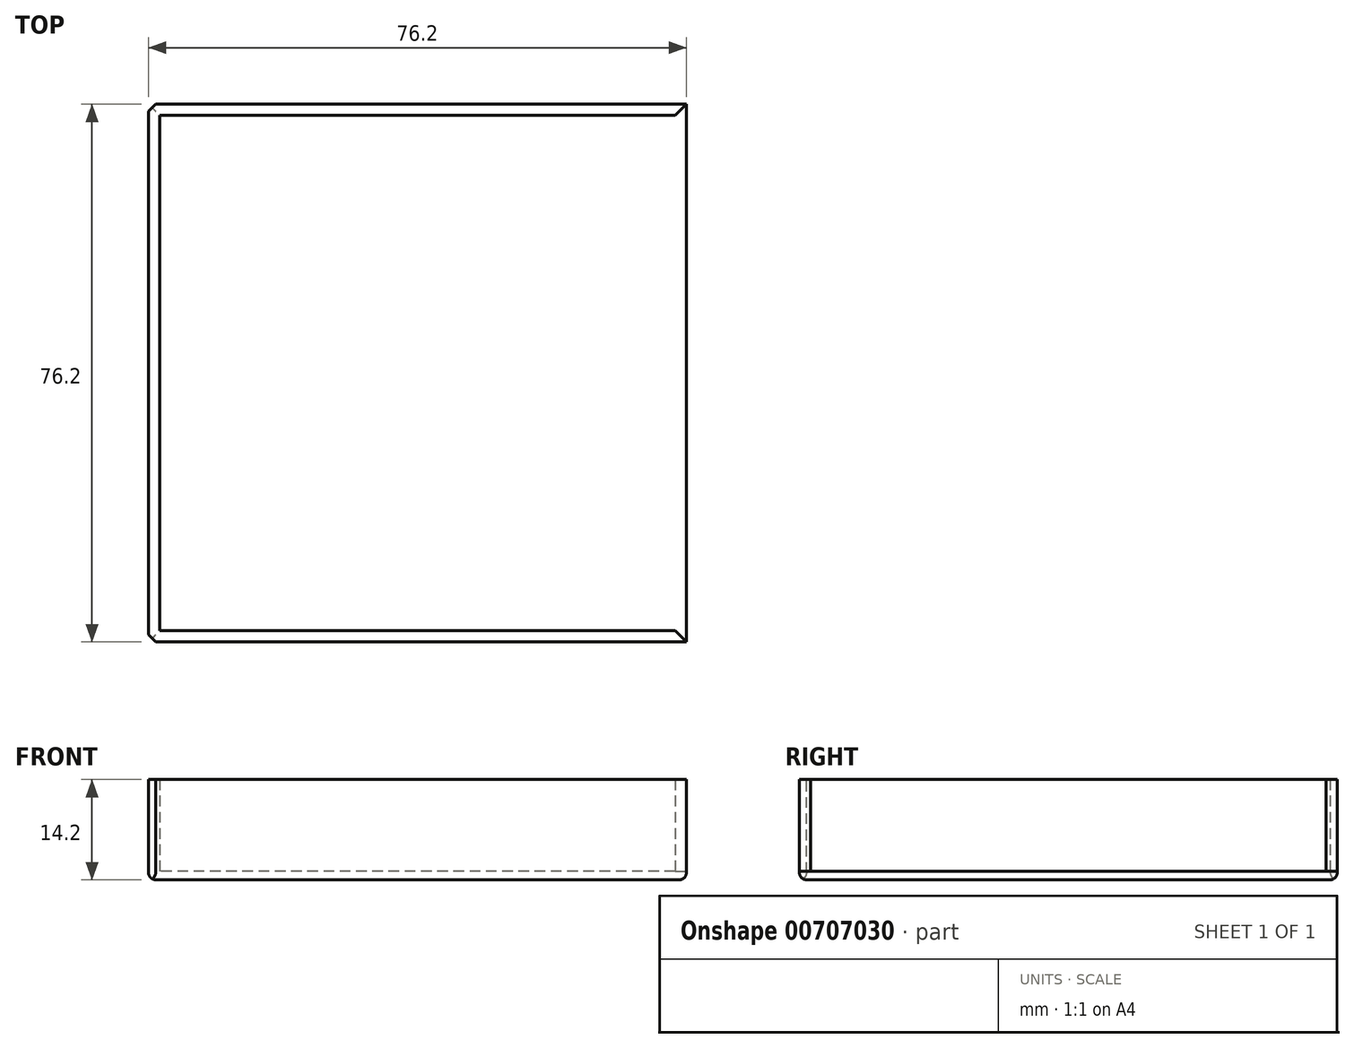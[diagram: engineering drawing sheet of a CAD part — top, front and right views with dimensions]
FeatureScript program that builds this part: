
annotation { "Feature Type Name" : "Feature", "Feature Type Description" : "" }
export const myFeature = defineFeature(function(context is Context, id is Id, definition is map)
    precondition{}
    {
        {
            var Q0;
            Q0=qCreatedBy(makeId("Top.planeOp"),FACE);
            var sketch = newSketch(context, id + "F0", { "sketchPlane" : qUnion([Q0])});
            skLineSegment(sketch, "E0.bottom", {"start": v(36.5, 36.5) * mm, "end": v(-36.5, 36.5) * mm});
            skLineSegment(sketch, "E0.top", {"start": v(36.5, -36.5) * mm, "end": v(-36.5, -36.5) * mm});
            skLineSegment(sketch, "E0.right", {"start": v(-36.5, 36.5) * mm, "end": v(-36.5, -36.5) * mm});
            skPoint(sketch, "E0.middle", {"position": v(0, 0) * mm});
            skLineSegment(sketch, "E1.bottom", {"start": v(38.1, 38.1) * mm, "end": v(-38.1, 38.1) * mm});
            skLineSegment(sketch, "E1.top", {"start": v(38.1, -38.1) * mm, "end": v(-38.1, -38.1) * mm});
            skLineSegment(sketch, "E1.right", {"start": v(-38.1, 38.1) * mm, "end": v(-38.1, -38.1) * mm});
            skLineSegment(sketch, "E2", {"start": v(36.5, 36.5) * mm, "end": v(38.1, 38.1) * mm});
            skLineSegment(sketch, "E3", {"start": v(36.5, -36.5) * mm, "end": v(38.1, -38.1) * mm});
            skSolve(sketch);
        }
        {
            var Q0;
            Q0=makeQuery(id+"F0.imprint","IMPRINT",FACE,{"disambiguationData":[TD([[makeQuery(id+"F0.imprint","IMPRINT",EDGE,{"derivedFrom":sQuery(id+"F0.wireOp",EDGE,"E0.bottom")}),-1.0]])]});
            extrude(context, id + "F1", {"entities" : qUnion([Q0]), "depth" : 13 * mm, "offsetDistance" : 25 * mm});
        }
        {
            var Q0;
            Q0=qCreatedBy(makeId("Top.planeOp"),FACE);
            var sketch = newSketch(context, id + "F2", { "sketchPlane" : qUnion([Q0])});
            skLineSegment(sketch, "E4.bottom", {"start": v(38.1, 38.1) * mm, "end": v(-38.1, 38.1) * mm});
            skLineSegment(sketch, "E4.top", {"start": v(38.1, -38.1) * mm, "end": v(-38.1, -38.1) * mm});
            skLineSegment(sketch, "E4.left", {"start": v(38.1, 38.1) * mm, "end": v(38.1, -38.1) * mm});
            skLineSegment(sketch, "E4.right", {"start": v(-38.1, 38.1) * mm, "end": v(-38.1, -38.1) * mm});
            skPoint(sketch, "E4.middle", {"position": v(0, 0) * mm});
            skSolve(sketch);
        }
        {
            var Q0;
            Q0=makeQuery(id+"F2.imprint","IMPRINT",FACE,{"disambiguationData":[TD([[makeQuery(id+"F2.imprint","IMPRINT",EDGE,{"derivedFrom":sQuery(id+"F2.wireOp",EDGE,"E4.bottom")}),1.0]])]});
            extrude(context, id + "F3", {"entities" : qUnion([Q0]), "operationType" : NewBodyOperationType.ADD, "oppositeDirection" : true, "depth" : 1.2 * mm, "offsetDistance" : 25 * mm});
        }
        {
            var Q0;
            Q0=makeQuery(id+"F3.opExtrude","CAP_EDGE",EDGE,{"disambiguationData":[OSD([sQuery(id+"F2.wireOp",EDGE,"E4.top")])],"isStart":false});
            var Q1;
            Q1=makeQuery(id+"F3.opExtrude","CAP_EDGE",EDGE,{"disambiguationData":[OSD([sQuery(id+"F2.wireOp",EDGE,"E4.left")])],"isStart":false});
            var Q2;
            Q2=makeQuery(id+"F3.opExtrude","CAP_EDGE",EDGE,{"disambiguationData":[OSD([sQuery(id+"F2.wireOp",EDGE,"E4.bottom")])],"isStart":false});
            var Q3;
            Q3=makeQuery(id+"F3.opExtrude","CAP_EDGE",EDGE,{"disambiguationData":[OSD([sQuery(id+"F2.wireOp",EDGE,"E4.right")])],"isStart":false});
            fillet(context, id + "F4", {"entities" : qUnion([Q0, Q1, Q2, Q3]), "radius" : 1 * mm, "tangentPropagation" : true, "allowEdgeOverflow" : false});
        }
        {
            var Q0;
            Q0=makeQuery(id+"F3.boolean.opBoolean","MERGE",EDGE,{"derivedFrom":[makeQuery(id+"F1.opExtrude","SWEPT_EDGE",EDGE,{"disambiguationData":[OSD([sQuery(id+"F0.wireOp",EDGE,"E1.top"),sQuery(id+"F0.wireOp",EDGE,"E1.right")])]}),makeQuery(id+"F3.opExtrude","SWEPT_EDGE",EDGE,{"disambiguationData":[OSD([sQuery(id+"F2.wireOp",EDGE,"E4.top"),sQuery(id+"F2.wireOp",EDGE,"E4.right")])]})]});
            var Q1;
            Q1=makeQuery(id+"F3.boolean.opBoolean","MERGE",EDGE,{"derivedFrom":[makeQuery(id+"F1.opExtrude","SWEPT_EDGE",EDGE,{"disambiguationData":[OSD([sQuery(id+"F0.wireOp",EDGE,"E1.bottom"),sQuery(id+"F0.wireOp",EDGE,"E1.right")])]}),makeQuery(id+"F3.opExtrude","SWEPT_EDGE",EDGE,{"disambiguationData":[OSD([sQuery(id+"F2.wireOp",EDGE,"E4.bottom"),sQuery(id+"F2.wireOp",EDGE,"E4.right")])]})]});
            chamfer(context, id + "F5", {"entities" : qUnion([Q0, Q1]), "width" : 1 * mm});
        }
    });
